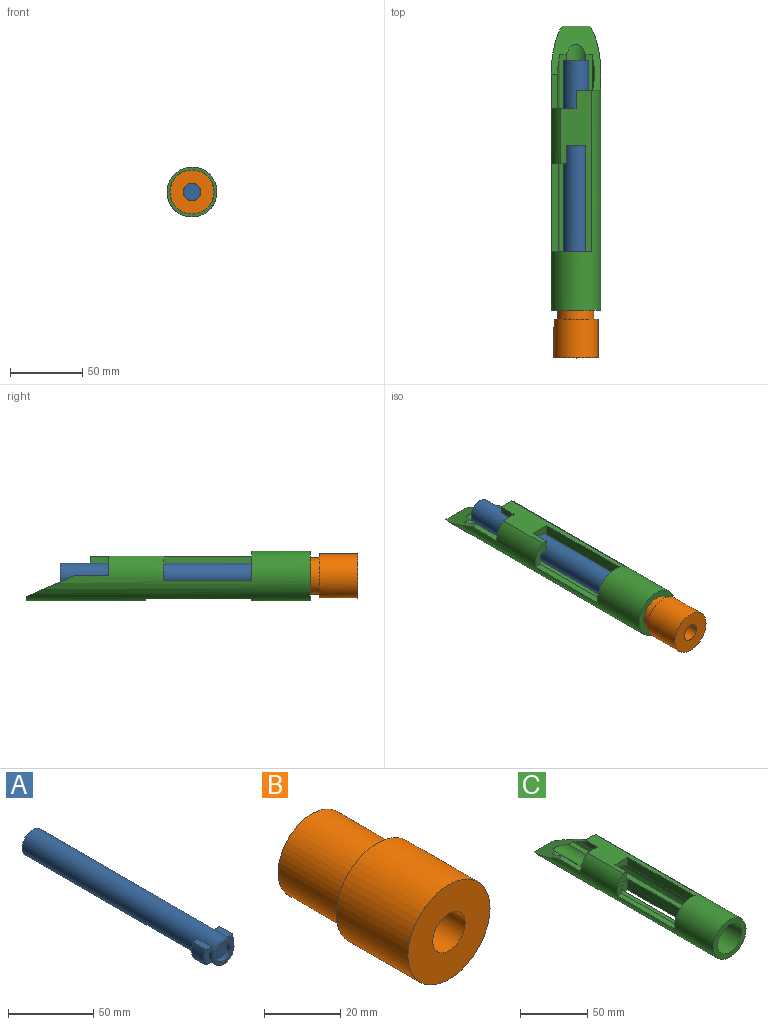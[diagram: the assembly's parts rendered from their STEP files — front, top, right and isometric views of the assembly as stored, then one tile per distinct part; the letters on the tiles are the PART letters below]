
ASSEMBLY  parts=3 mates=3
PART A: 21 faces, bbox 24.9x158.8x17.5 mm
  f0: cylinder r=8.76mm len=158.24mm, axis (0,1,0), area 8441.9mm2, adj f2,f6,f7,f8,f9,f10,f11,f12
  f1: plane 16.51x16.51mm, normal (0,-1,0), area 77.1mm2, adj f15,f16
  f2: plane 17.53x17.53mm, normal (0,1,0), area 241.2mm2, adj f0
  f3: cylinder r=6.1mm len=12.19mm, axis (0,-1,0), area 126.5mm2, adj f4,f15
  f4: plane 12.19x12.19mm, normal (0,-1,0), area 116.7mm2, adj f3
  f5: cylinder r=12.45mm len=11.18mm, axis (0,-1,0), area 117.8mm2, adj f8,f9,f17,f18
  f6: plane 11.18x5.19mm, normal (0,1,0), area 37.6mm2, adj f0,f8,f9,f17
  f7: plane 11.18x5.19mm, normal (0,-1,0), area 37.6mm2, adj f0,f8,f9,f18
  f8: plane 11.18x4.38mm, normal (0,0,1), area 48.6mm2, adj f0,f5,f6,f7,f17,f18
  f9: plane 11.18x4.38mm, normal (0,0,-1), area 48.6mm2, adj f0,f5,f6,f7,f17,f18
  f10: plane 11.18x4.38mm, normal (0,0,-1), area 48.6mm2, adj f0,f12,f13,f14,f19,f20
  f11: plane 11.18x4.38mm, normal (0,0,1), area 48.6mm2, adj f0,f12,f13,f14,f19,f20
  f12: plane 11.18x5.19mm, normal (0,1,0), area 37.6mm2, adj f0,f10,f11,f19
  f13: plane 11.18x5.19mm, normal (0,-1,0), area 37.6mm2, adj f0,f10,f11,f20
  f14: cylinder r=12.45mm len=11.18mm, axis (0,-1,0), area 117.8mm2, adj f10,f11,f19,f20
  f15: cone r=6.1mm half-angle=45deg, axis (0,-1,0), area 28.7mm2, adj f1,f3
  f16: cone r=8.26mm half-angle=45deg, axis (0,1,0), area 38.4mm2, adj f0,f1
  f17: cone r=12.45mm half-angle=45deg, axis (0,-1,0), area 8.3mm2, adj f5,f6,f8,f9
  f18: cone r=11.94mm half-angle=45deg, axis (0,1,0), area 8.3mm2, adj f5,f7,f8,f9
  f19: cone r=12.45mm half-angle=45deg, axis (0,-1,0), area 8.3mm2, adj f10,f11,f12,f14
  f20: cone r=11.94mm half-angle=45deg, axis (0,1,0), area 8.3mm2, adj f10,f11,f13,f14
PART B: 8 faces, bbox 30.5x50.8x30.5 mm
  f0: cylinder r=5.99mm len=46.99mm, axis (0,1,0), area 1769.8mm2, adj f3,f7
  f1: plane 25.4x25.4mm, normal (0,1,0), area 258.4mm2, adj f5,f6
  f2: cylinder r=15.24mm len=30.48mm, axis (0,1,0), area 2553.8mm2, adj f3,f4
  f3: plane 30.48x30.48mm, normal (0,-1,0), area 616.8mm2, adj f0,f2
  f4: plane 30.48x30.48mm, normal (0,1,0), area 223mm2, adj f2,f5
  f5: cylinder r=12.7mm len=25.4mm, axis (0,1,0), area 1925.5mm2, adj f1,f4
  f6: cylinder r=8.89mm len=17.78mm, axis (0,1,0), area 212.8mm2, adj f1,f7
  f7: plane 17.78x17.78mm, normal (0,1,0), area 135.4mm2, adj f0,f6
PART C: 31 faces, bbox 34.5x196.9x34.5 mm
  f0: plane 111.76x20.99mm, normal (0,0,1), area 991.8mm2, adj f2,f5,f15,f17,f18,f20,f27,f28
  f1: plane 38.1x4.53mm, normal (0,0,-1), area 172.7mm2, adj f3,f6,f17,f30
  f2: plane 12.7x7.91mm, normal (1,0,0), area 100.4mm2, adj f0,f3,f27,f30
  f3: cylinder r=8.89mm len=123.19mm, axis (0,1,0), area 680.4mm2, adj f1,f2,f8,f9,f10,f15,f17,f18
  f4: cylinder r=8.89mm len=154.96mm, axis (0,1,0), area 1239.8mm2, adj f12,f13,f14,f21,f23,f24,f25,f26
  f5: cylinder r=17.27mm len=196.85mm, axis (0,1,0), area 13550.1mm2, adj f0,f7,f11,f15,f16,f17,f19,f20
  f6: cylinder r=12.7mm len=176.8mm, axis (0,-1,0), area 4848.7mm2, adj f1,f8,f9,f10,f11,f12,f13,f14
  f7: plane 19.12x2.89mm, normal (0,1,0), area 37.5mm2, adj f5,f21
  f8: plane 123.19x4.53mm, normal (0,0,-1), area 558.3mm2, adj f3,f6,f10,f20
  f9: plane 11.43x4.53mm, normal (0,0,-1), area 51.8mm2, adj f3,f6,f10,f15
  f10: plane 22.68x6.99mm, normal (0,-1,0), area 83.2mm2, adj f3,f6,f8,f9
  f11: plane 34.54x34.54mm, normal (0,-1,0), area 430.5mm2, adj f5,f6
  f12: plane 22.68x6.99mm, normal (0,-1,0), area 83.2mm2, adj f4,f6,f13,f14
  f13: plane 147.59x4.53mm, normal (0,0,1), area 668.9mm2, adj f4,f6,f12,f21
  f14: plane 147.59x4.53mm, normal (0,0,1), area 668.9mm2, adj f4,f6,f12,f21
  f15: plane 27.77x20.62mm, normal (0,1,0), area 228.9mm2, adj f0,f3,f5,f6,f9,f28,f29
  f16: plane 23.89x4.57mm, normal (0,0,1), area 109.2mm2, adj f5,f6,f17,f21
  f17: plane 17.27x13.72mm, normal (0,1,0), area 123.8mm2, adj f0,f1,f3,f5,f6,f16,f18
  f18: plane 12.7x4.83mm, normal (-1,0,0), area 61.3mm2, adj f0,f3,f17,f20
  f19: plane 4.84x0.05mm, normal (0,0,1), area 0.3mm2, adj f5,f6,f20,f22
  f20: plane 16.58x8.89mm, normal (0,1,0), area 101.3mm2, adj f0,f3,f5,f6,f8,f18,f19
  f21: plane 44.4x34.54mm, normal (0,0.4,0.92), area 714mm2, adj f4,f5,f6,f7,f13,f14,f16,f22
  f22: plane 4.84x0.01mm, normal (0,0.99,-0.16), area 0.1mm2, adj f5,f6,f19,f21
  f23: plane 13.46x11.46mm, normal (0,-1,0), area 119.5mm2, adj f4,f5,f24,f26
  f24: plane 73.66x10.1mm, normal (-1,0,0), area 743.9mm2, adj f4,f5,f23,f25
  f25: plane 13.46x11.46mm, normal (0,1,0), area 119.5mm2, adj f4,f5,f24,f26
  f26: plane 73.66x10.1mm, normal (1,0,0), area 743.9mm2, adj f4,f5,f23,f25
  f27: plane 13.46x7.91mm, normal (0,-1,0), area 77.7mm2, adj f0,f2,f3,f28
  f28: plane 73.66x7.91mm, normal (-1,0,0), area 582.5mm2, adj f0,f3,f15,f27
  f29: plane 60.96x4.69mm, normal (0,0,1), area 286.1mm2, adj f5,f6,f15,f30
  f30: plane 17.06x10.54mm, normal (0,-1,0), area 100.4mm2, adj f0,f1,f2,f3,f5,f6,f29
PLACE A rot(axis=(0,-1,0),90deg) t=(-34.34,-118.89,-4.71)mm
PLACE B t=(-34.34,-274.08,-4.71)mm
PLACE C rot(axis=(0,1,0),0deg) t=(-34.34,-95.01,-4.71)mm
MATE cylindrical C.f6 <-> B.f5  axis (0,-1,0) through (-34.34,-202.93,-4.71)mm
MATE slider C.f3 <-> A.f0  axis (0,-1,0) through (-34.34,-262.65,-4.71)mm
MATE fastened A.f0 <-> C.f3  axis (0,1,0) through (-34.34,-262.65,-4.71)mm
